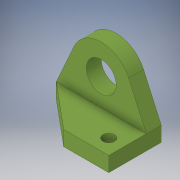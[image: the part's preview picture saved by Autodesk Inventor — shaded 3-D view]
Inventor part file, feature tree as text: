
AUTODESK INVENTOR PART (.ipt)
format: ipt  version: 2018 (Build 220112000, 112)  size: 145,408 bytes
history: native  units: in
note: dims shown in document units (in); Inventor stores cm internally (conversion verified against a paired STEP export)
features: extrude x4, sketch x4, projected_geometry x3, other x3, reference x1
ambient origin geometry x8: Origin, YZ Plane, XZ Plane, XY Plane, X Axis, Y Axis, Z Axis, Center Point
bodies: Solid1 (feature_tree)
feature tree (15):
  extrude  "Extrusion1"  Depth=0.195in
  extrude  "Extrusion2"  Depth=0.25in
  extrude  "Extrusion3"  Depth=0.25in
  extrude  "Extrusion4"  Depth=0.25in TaperAngle=0.0deg
  sketch  "Sketch1"  dims[d0=0.195in d1=0.195in]
  sketch  "Sketch2"  dims[d2=1.0in d3=0.25in]
  projected_geometry  "Projected Loop1"
  reference  "Reference1"
  sketch  "Sketch3"  dims[d4=0.125in d5=0.25in]
  projected_geometry  "Projected Loop2"
  sketch  "Sketch4"  dims[d6=0.75in d7=0.25in d8=0.0in d9=0.25in d10=0.5in d11=0.25in d12=0.0in d13=0.125in d14=0.0in d15=1.0in d16=0.0in]
  projected_geometry  "Projected Loop3"
  parser-record x1  (decoder bookkeeping rows leaked as tree rows — omitted from the tree; the rows remain in map.json)
  other  "Assembly2.iam"
  other  "0_375_Hex_ID_x_1_125_OD_x_0_313_WD_Flanged_Bearing_217-2735:2"
note: 1 file-system path scrubbed to <path> (originals preserved in map.json)
